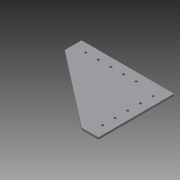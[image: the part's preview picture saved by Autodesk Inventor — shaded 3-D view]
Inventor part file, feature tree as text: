
AUTODESK INVENTOR PART (.ipt)
format: ipt  version: 2015 SP1 (Build 190203100, 203)  size: 130,560 bytes
history: native  units: in
note: dims shown in document units (in); Inventor stores cm internally (conversion verified against a paired STEP export)
features: other x3, hole x1, sketch x1
ambient origin geometry x8: Origin, YZ Plane, XZ Plane, XY Plane, X Axis, Y Axis, Z Axis, Center Point
bodies: Solid1 (feature_tree)
feature tree (5):
  other  "<userpath>\Documents\2015 Offseason Chassis\West Coast Chassis Fall 2015\rivet(rv).xlsx"
  hole  "Hole1"  [1 undecoded]
  other  "face_sketch"
  other  "Plate1"
  sketch  "Sketch4"  dims[d0=4.5in d2=1.0in d3=1.0in d4=0.12in d5=4.5in d6=0.1406in d7=0.75in d8=0.375in d9=0.25in d10=0.5635in d11=0.12in d12=0.8108in]
note: 1 required parameter value undecoded (feature->parameter linkage not recoverable at this tier; creation-order binding heuristic only, values carry confidence <= 0.55)
